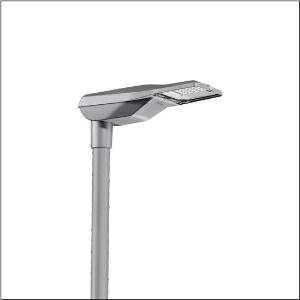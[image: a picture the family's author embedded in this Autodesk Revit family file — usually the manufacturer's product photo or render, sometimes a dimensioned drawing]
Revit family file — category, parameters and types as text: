
# Revit family: streetlight_sl_21_iq_micro___st1_0a_5xe1d21g08cb_51d7
name_source: partatom
category: Lighting Fixtures
units: mm (PartAtom-declared; Revit-internal decimal feet)

## family parameters
Cut with Voids When Loaded = No
Host = Face
Light Source = No
Part Type = Normal
Room Calculation Point = No
Round Connector Dimension = Use Diameter
Shared = No

## types (1)
- --- (1 x LED, 2380 lm, 19.4 W, 2200K)
    Apparent Load = 19 VA
    CIE Flux Codes = 37 72 97 100 100
    Color Rendering = 70
    Color Temperature = 2200K
    Default Elevation = 1800 mm
    Description = Streetlight SL 21 iQ micro, mast luminaire, primary light control with lens, of PMMA, primary optical cover: cover, of toughened safety glass, transparent, light distribution: ST1.0a, light emission: direct distribution, primary light characteristic: asymmetric, installation type: post-top, side-entry, LED, High Power LED, rated luminous flux: 2.380lm, luminous efficacy: 123lm/W, light colour: 722, colour temperature: 2200K, control: Street-Remote, Auto-Match, Temp-Guard, Lumen-Switch, Night-Set, Smart-Wire, Light-Fading, Desk-Remote (wireless, voltage-free reading and setting of iQ features in the workshop via application-optimized NFC function/RFID function), optimised constant luminous flux control (CLO 2.0), presetting dimming linear, mains connection: 220..240V, AC, 50/60Hz, start of lifetime: 19W, end of service life: 20W, reduction: 10W, luminaire housing, of diecast aluminium, powder-coated, Siteco® metallic grey (DB 702S), corrosivity category C5 mid according to DIN EN ISO 12944, please order mast flange separately, inclination adjustable: 0°, 5°, 10°, 15°, sealing non-destructively replaceable, multi-level sealing system, length: 528mm, width: 235mm, height: 110mm, mast flange for spigot size: 42mm (side-entry): 5XC10008XM4, 60/48mm (side-entry/post-top): 5XC10108XM2, 76/60mm (side-entry/post-top): 5XC10108XM1, protection rating (complete): IP66, insulation class (complete): insulation class II (safety insulation), certification: CE, ENEC, ENEC+, VDE, impact resistance: IK09, permissible operating ambient temperature for outdoor applications: -40..+50°C, standard-compliant lighting for roads and squares, packaging unit: 1 piece

Light Distribution: ST1.0a
    Height = 110 mm
    Lamp = 1 x LED
    Lamp Light Flux = 2380 lm
    Lamp Power = 19.4 W
    Lamp count = 1
    Length = 528 mm
    Luminous efficacy = 123 lm/W
    Manufacturer = Siteco
    ModVariant = No
    Model = 5XE1D21G08CB
    Number of Poles = 1
    OnlyDefault = Yes
    Power Factor = 1
    Product Name = Streetlight SL 21 iQ micro | ST1.0a
    Product group = mast luminaire | pylon top
    ProductGroupID = 6100
    Protection Class = Protection class II
    Protection Degree = IP 66
    RLX_Detail_Level = 1
    RLX_Emergency_Light_Flux = 0 lm
    RLX_Emergency_Type = 0
    RLX_Emergency_Type_DB = No
    RlxData = <blob elided: 98721 chars, md5=5d649c57>
    Socket = socket
    Standby Power = 0 W
    System Light Flux = 2380 lm
    System Power = 19 W
    Type Comments = factory setting: luminous flux: 100 % | dim-lin: 254 | 387 mA
    Type Image = l_1006881.jpg
    URL = http://relux.com
    VarID = @adj_070649
    Voltage = 0 V
    Weight = 0.00 kg
    Width = 235 mm

## geometry (parser evidence)
native form markers: Blend x4, Sweep x11
no freeform markers — native parametric forms only
